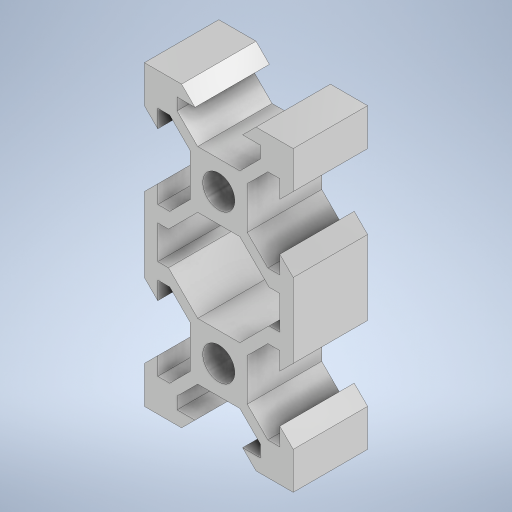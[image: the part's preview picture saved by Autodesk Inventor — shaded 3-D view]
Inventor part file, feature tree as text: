
AUTODESK INVENTOR PART (.ipt)
format: ipt  version: 2024.2 (Build 282272000, 272)  size: 412,672 bytes
history: native  units: mm
features: extrude x2, sketch x2, pattern_linear x1
ambient origin geometry x8: Origin, YZ Plane, XZ Plane, XY Plane, X Axis, Y Axis, Z Axis, Center Point
bodies: Solid1 (feature_tree)
feature tree (5):
  extrude  "Extrusion1"  Depth=10.0mm
  pattern_linear  "Rectangular Pattern1"  Spacing1=4.4mm  [1 undecoded]
  extrude  "Extrusion2"  TaperAngle=45.0deg  [1 undecoded]
  sketch  "Sketch1"  dims[d16=10.0mm d19=3.2mm]
  sketch  "Sketch2"  dims[d21=4.4mm d22=4.4mm d24=45.0deg d25=1.8mm d27=1.8mm d28=45.0deg d29=3.2mm d31=1.4mm d33=2.15mm d34=3.825mm d35=3.825mm d36=135.0deg d37=40.0mm d39=360.0deg d41=10.0mm d42=0.0mm d43=20.0mm d45=20.0mm d46=4.5mm d48=0.0mm d49=0.0mm d50=1.8mm d51=0.5mm d52=0.872665mm d53=0.5mm d54=0.872665mm]
note: 2 required parameter values undecoded (feature->parameter linkage not recoverable at this tier; creation-order binding heuristic only, values carry confidence <= 0.55)
